# Revit family: Quantum_Odyssey_CBS2LEDS-DIF-xx_Non-Hosted_R16
name_source: partatom
category: Lighting Fixtures
revit_build: Autodesk Revit 2016 (Build: 20151007_0715(x64)
units: mm (PartAtom-declared; Revit-internal decimal feet)

## family parameters
Always vertical = Yes
Cut with Voids When Loaded = No
Light Source = Yes
OmniClass Number = 23.80.70.00
OmniClass Title = Lighting
Part Type = Normal
Room Calculation Point = No
Round Connector Dimension = Use Diameter
Shared = No
Work Plane-Based = No

## types (7) — shared parameters
AS2293 Classification = C0=D40 C90=D40
Battery = 3.2V 3200mAh
Battery Type = Lithium Iron Phosphate
Charging Method = Intelligent Current Limited Constant Voltage
Color Filter = 16777215
Construction = Powder Coated Steel Body and PC/ABS End Caps
Diffuser = Acrylic Prismatic Diffuse
Dimensions (L x W x H) = 664mm x 120mm x 108mm
Dimming Lamp Color Temperature Shift = <None>
Emergency Lumen Output = 249.6lm
Emit Shape Visible in Rendering = No
IP Rating = IP20
Lamp = LED Strip Module, 4,000K Natural White, 50,000h Life [L70/B50 Ta 40°C], Ra>80
Manufacturer = Clevertronics
Mounting = Surface Mount
Operating Mode = Sustained
Operating Temperature = 1°C to 40°C
Operating Voltage = 240V AC; 50Hz
Photometric Web File = ll22528_CBS4LEDS-DIF-ZW(AUB02110010002,AS2293.3,Photometry).ies
Power Factor = 0.95
Replacement Battery = 1550050 Battery, LP 3.2V 3200mAh 70mm lead, no Bracket
Replacement lamp = 8002695 PCA:LED Strip 8S6P, ALS-13-840-0-02-B
Tilt Angle = 90.00°
Weight = 2.0 kg

## per-type parameters (varying)
| type | Applicable Standards | Description | LED Driver | MIC Number | Power Consumption | Power Consumption (Standby - Lamp Off) | Power Consumption (Standby - Lamp On) | Replacement Driver | Replacement Emergency Driver | Replacement Item | Sensor | Testing System | Total Lumen Output |
| CBS2LEDS-DIF |  | LP Premium Quantum 600mm LED Diffused Batten with LED Emergency Pod, enabled
with Clevertest Plus | Osram 40W, 500-1050mA, 15-50V | AUB02310060001 | 20W | 0.4W |  | 1330029 LED XZ Driver – 40w 500mA, 15-50V | CLIFE-CKIT-NP Lifelight, Control Only, LP, CTP, No Plug |  |  | Clevertest Plus Enabled (Not activated by default) | 2200lm @ 105lm/W |
| CBS2LEDS-DIF-DALI |  | LP Premium Odyssey Quantum LED 600mm Diffused Batten with LED Emergency Pod | Osram 40W, 500-1050mA, 15-50V | AUB02211090002 | 25W | 1W | 22W | 1330029 LED XZ Driver – 40w 500mA, 15-50V | AUM02270170002
CLIFE-CKIT-DALI-NP Lifelight, Control Only, Dali Reg, LP, No Plug (incl. DALI Node) |  |  | DALI Registered | 2187lm @ 105lm /W |
| CBS2LEDS-DIF-DD-DALI |  | LP Premium Quantum LED Diffused Batten with Dali Driver and LED Emergency Pod
with Clevertest Plus | LED DALI Driver - 25W, 350-1050mA, 20-50V, one4all | AUB02211020001 | 24W | 0.4W | 22W | 1330038 LED DALI Driver - 25W, 350-1050mA, 20-50V, one4all | CLIFE-CKIT-NP Lifelight, Control Only, LP, CTP, No Plug |  |  | DALI Registered | 2187lm @ 99 lm/W |
| CBS2LEDS-DIF-HV | AS/NZS3820, CISPR15, AS/NZS2293.3 | LP Premium Quantum 600mm LED Diffused Batten with LED Emergency Pod
with Clevertest Plus | Osram 40W, 500-1050mA, 15-50V (700mA) | AUB02810020002 | 25W | 1.2W | 20W | 1330029 LED XZ Driver – 40W, 500-1050mA, 15-50V, 700mA | AUM02870100001 CLIFE-CKIT-HVEXTA-NP Lifelight, Control Only, HV, LP, No Plug (incl. Hive node) |  |  | Zoneworks XT HIVE (RF) | 2187lm @ 105lm/W |
| CBS2LEDS-DIF-MS | AS/NZS3820, CISPR15, AS/NZS2293.3 | LP Odyssey Quantum LED Diffused Batten with LED Emergency Pod and Microwave Sensor, Enabled with Clevertest Plus
with Clevertest Plus | 40w, 500-1050mA, 15-50V | AUB02310070001 | 27W | 1.5W | 19W | 1330029 LED XZ Driver – 40W, 500-1050mA, 15-50V, 700mA | CLIFE-CKIT-NP Lifelight, Control Only, LP, No Plug |  | 1190117 SENSOR: Microwave Motion IP20 MC602S | Clevertest Plus Enabled (Not activated by default) | 2187lm @102lm/W |
| CBS2LEDS-DIF-MS-HV | AS/NZS3820, CISPR15, AS/NZS2293.3 | LP Premium Quantum LED diffused batten with LED Emergency Pod and microwave sensor control of the lamps (on/off) | 40w, 500-1050mA, 15-50V | AUB02810120001 | 24W | 1W | 21W | 1330029 LED XZ Driver – 40W, 500-1050mA, 15-50V, 700mA | CLIFE-CKIT-NP Lifelight, Control Only, LP, No Plug | 8001390 PCA: RF Node CT10678-Ax internal antenna | 1190117 SENSOR: Microwave Motion IP20 MC602S | Zoneworks XT HIVE (RF) | 2187lm |
| CBS2LEDS-DIF-ZW | AS/NZS3820, CISPR15, AS/NZS2293.3 | LP Premium Quantum 600mm LED Diffused Batten with LED Emergency Pod | Osram 40W, 500-1050mA, 15-50V | AUB02110060001 | 20W | 0.4W |  | 1330029 LED XZ Driver – 40W, 500-1050mA, 15-50V, 700mA | CLIFE-CKIT-NP Lifelight, Control Only, LP, No Plug | 8001450 PCA:Powerline Node ZW, #CT10310-A6 |  | Zoneworks Computerised Testing | 2200lm @ 105lm/W |

note: column(s) folded — value = type name in every type: Model

## geometry (parser evidence)
native form markers: Sweep x2
no freeform markers — native parametric forms only
